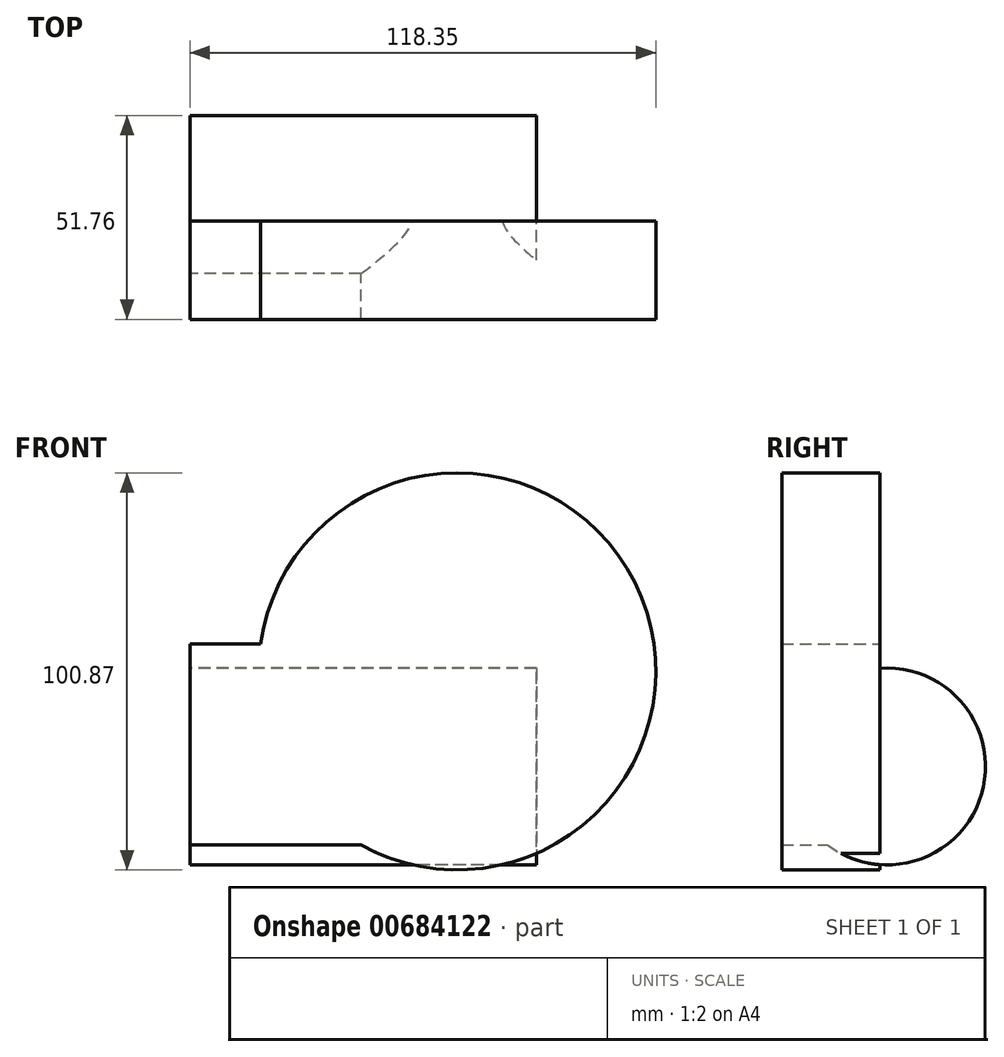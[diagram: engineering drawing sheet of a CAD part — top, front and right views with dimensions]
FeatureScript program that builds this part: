
annotation { "Feature Type Name" : "Feature", "Feature Type Description" : "" }
export const myFeature = defineFeature(function(context is Context, id is Id, definition is map)
    precondition{}
    {
        {
            var Q0;
            Q0=qCreatedBy(makeId("Front.planeOp"),FACE);
            var sketch = newSketch(context, id + "F0", { "sketchPlane" : qUnion([Q0])});
            skLineSegment(sketch, "E0.bottom", {"start": v(71.52, 51.03) * mm, "end": v(0, 51.03) * mm});
            skLineSegment(sketch, "E0.top", {"start": v(71.52, 0) * mm, "end": v(0, 0) * mm});
            skLineSegment(sketch, "E0.left", {"start": v(71.52, 51.03) * mm, "end": v(71.52, 0) * mm});
            skLineSegment(sketch, "E0.right", {"start": v(0, 51.03) * mm, "end": v(0, 0) * mm});
            skSolve(sketch);
        }
        {
            var Q0;
            Q0 = qSketchRegion(id + "F0", true);
            extrude(context, id + "F1", {"entities" : qUnion([Q0]), "depth" : 25 * mm, "offsetDistance" : 25 * mm});
        }
        {
            var Q0;
            Q0=qCreatedBy(makeId("Right.planeOp"),FACE);
            var sketch = newSketch(context, id + "F2", { "sketchPlane" : qUnion([Q0])});
            skCircle(sketch, "E1", {"center": v(1.76, 19.92) * mm, "radius": 25 * mm});
            skSolve(sketch);
        }
        {
            var Q0;
            Q0 = qSketchRegion(id + "F2", true);
            extrude(context, id + "F3", {"entities" : qUnion([Q0]), "operationType" : NewBodyOperationType.ADD, "depth" : 88 * mm, "offsetDistance" : 25 * mm, "hasSecondDirection" : true, "secondDirectionOppositeDirection" : false, "secondDirectionDepth" : 0 * mm});
        }
        {
            var Q0;
            Q0=qCreatedBy(makeId("Front.planeOp"),FACE);
            var sketch = newSketch(context, id + "F4", { "sketchPlane" : qUnion([Q0])});
            skCircle(sketch, "E2", {"center": v(67.91, 44.1) * mm, "radius": 50.44 * mm});
            skSolve(sketch);
        }
        {
            var Q0;
            Q0 = qSketchRegion(id + "F4", true);
            extrude(context, id + "F5", {"entities" : qUnion([Q0]), "operationType" : NewBodyOperationType.ADD, "depth" : 25 * mm, "offsetDistance" : 25 * mm});
        }
    });
